# Revit family: FP_Revit_18_RF730QZUVB1_Fridge_90001899A
name_source: partatom
category: Specialty Equipment
revit_build: Autodesk Revit 2018 (Build: 20170223_1515(x64)
units: mm (PartAtom-declared; Revit-internal decimal feet)

## family parameters
Always vertical = Yes
Cut with Voids When Loaded = Yes
OmniClass Number = 23.40.40.11.11.17
OmniClass Title = Refrigerator-Freezer
Part Type = Normal
Room Calculation Point = No
Round Connector Dimension = Use Diameter
Shared = No
Work Plane-Based = No

## types (2) — shared parameters
Chassis - Depth = 663 mm  [stored 2.1752 ft]
Chassis - Height = 1867 mm  [stored 6.12533 ft]
Chassis - Width = 905 mm  [stored 2.96916 ft]
Connector Description - Electrical = 220-240 V, 50 Hz, 1.8 A,
Description = Freestanding Quad Door Refrigerator Freezer
Manufacturer = Fisher & Paykel Appliances
Material - Body = Fisher & Paykel - Grey
Material - Door Front = Fisher & Paykel - Stainless Steel, Dark
Material - Door Structure = Fisher & Paykel - White
Material - Glass = Fisher & Paykel - Grey
Material - Trim = Fisher & Paykel - Aluminium, Dark
Model = RF730QZUVB1
Product - Depth = 748 mm  [stored 2.45407 ft]
Product - Height = 1900 mm  [stored 6.2336 ft]
Product - Width = 905 mm  [stored 2.96916 ft]
URL = www.fisherpaykel.com
Visibility - Clearance Required = Yes

## per-type parameters (varying)
| type | Cavity - Depth | Cavity - Door Clearance | Cavity - Height | Cavity - Width | Connector Description - Water |
| RF730QZUVB1 (Proud) | 690 mm  [stored 2.26378 ft] | 350 mm  [stored 1.14829 ft] | 1920 mm  [stored 6.29921 ft] | 985 mm  [stored 3.23163 ft] | 13mm (1/2") or 19mm (3/4") BSP threaded water connection 6.35mm LLDPE tubing |
| RF730QZUVB1 (Flush) | 778 mm  [stored 2.55249 ft] | 260 mm  [stored 0.853018 ft] | 1945 mm  [stored 6.38123 ft] | 1125 mm | Min 150kPa (22psi), max 827kPa (120psi) @ 20°C |

note: [stored X ft] marks values corroborated as IEEE doubles in the binary element streams (Revit-internal decimal feet)

## geometry (parser evidence)
native form markers: Sweep x11
no freeform markers — native parametric forms only
